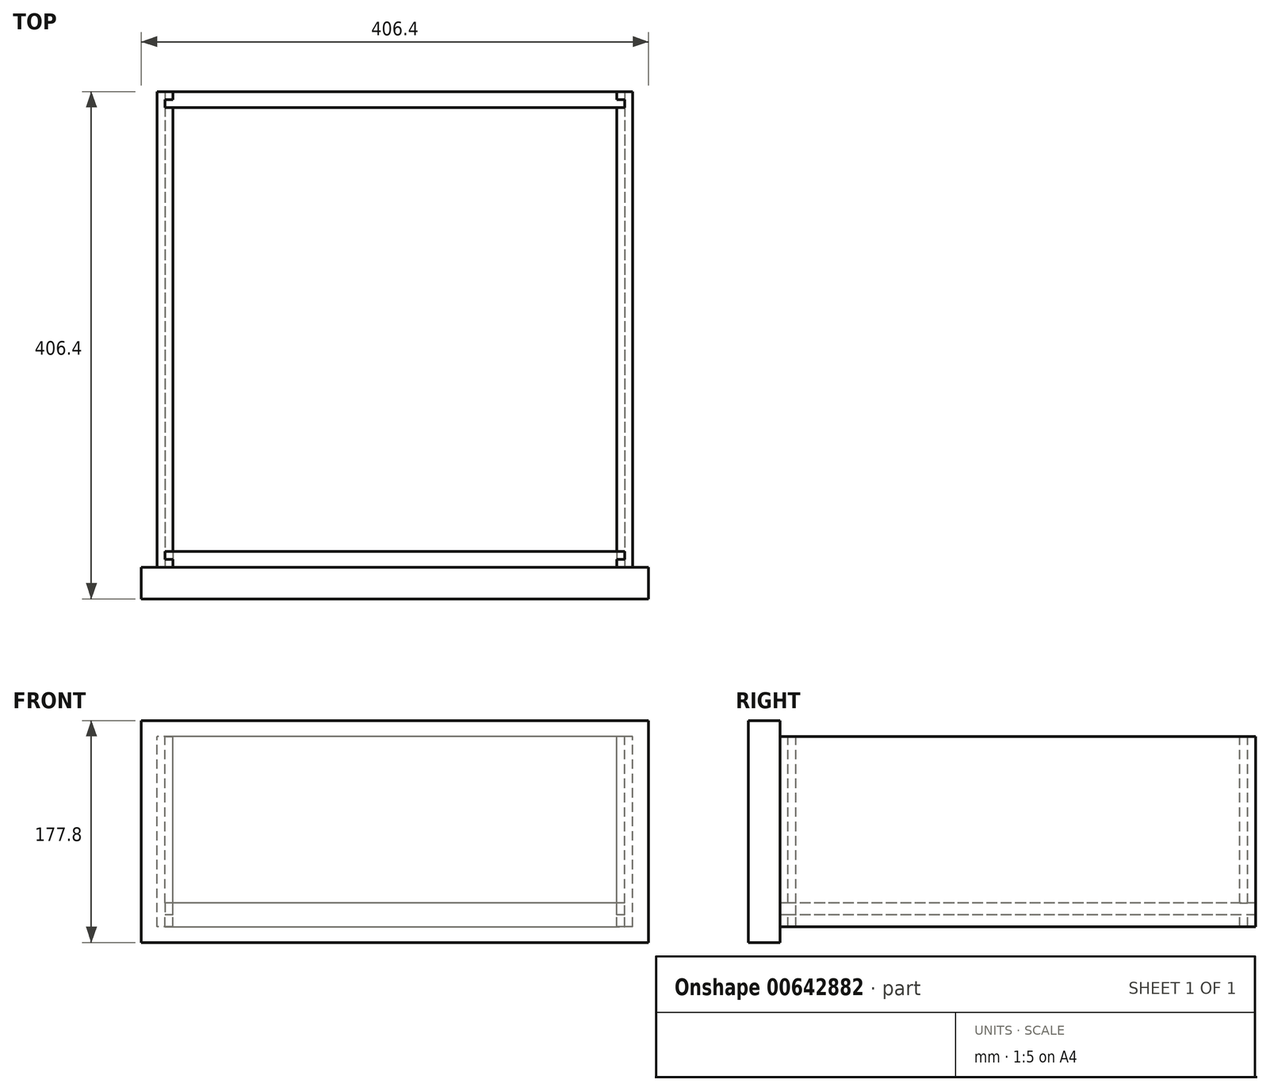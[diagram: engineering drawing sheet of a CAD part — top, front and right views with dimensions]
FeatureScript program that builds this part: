
annotation { "Feature Type Name" : "Feature", "Feature Type Description" : "" }
export const myFeature = defineFeature(function(context is Context, id is Id, definition is map)
    precondition{}
    {
        {
            var Q0;
            Q0=qCreatedBy(makeId("Top.planeOp"),FACE);
            var sketch = newSketch(context, id + "F0", { "sketchPlane" : qUnion([Q0])});
            skLineSegment(sketch, "E0.bottom", {"start": v(190.5, -190.5) * mm, "end": v(-190.5, -190.5) * mm});
            skLineSegment(sketch, "E0.top", {"start": v(190.5, 190.5) * mm, "end": v(-190.5, 190.5) * mm});
            skLineSegment(sketch, "E0.left", {"start": v(190.5, -190.5) * mm, "end": v(190.5, 190.5) * mm});
            skLineSegment(sketch, "E0.right", {"start": v(-190.5, -190.5) * mm, "end": v(-190.5, 190.5) * mm});
            skPoint(sketch, "E0.middle", {"position": v(0, 0) * mm});
            skLineSegment(sketch, "E1.0", {"start": v(-177.8, -190.5) * mm, "end": v(-177.8, -184.15) * mm});
            skLineSegment(sketch, "E2.0", {"start": v(177.8, 177.8) * mm, "end": v(-184.15, 177.8) * mm});
            skLineSegment(sketch, "E2.1", {"start": v(177.8, -177.8) * mm, "end": v(177.8, 177.8) * mm});
            skLineSegment(sketch, "E2.2", {"start": v(177.8, -177.8) * mm, "end": v(-184.15, -177.8) * mm});
            skPoint(sketch, "E3", {"position": v(-177.8, 184.15) * mm});
            skPoint(sketch, "E4", {"position": v(-184.15, 177.8) * mm});
            skLineSegment(sketch, "E5", {"start": v(-184.15, 177.8) * mm, "end": v(-184.15, 184.15) * mm});
            skLineSegment(sketch, "E6", {"start": v(-184.15, 184.15) * mm, "end": v(-177.8, 184.15) * mm});
            skLineSegment(sketch, "E7.trimOffspring", {"start": v(-177.8, 184.15) * mm, "end": v(-177.8, 190.5) * mm});
            skPoint(sketch, "E8.orphan", {"position": v(-190.5, 177.8) * mm});
            skLineSegment(sketch, "E9.MirrorCS", {"start": v(184.15, 184.15) * mm, "end": v(177.8, 184.15) * mm});
            skLineSegment(sketch, "E10.MirrorCS", {"start": v(184.15, 177.8) * mm, "end": v(184.15, 184.15) * mm});
            skLineSegment(sketch, "E11.MirrorCS", {"start": v(177.8, 184.15) * mm, "end": v(177.8, 190.5) * mm});
            skLineSegment(sketch, "E12", {"start": v(177.8, 177.8) * mm, "end": v(184.15, 177.8) * mm});
            skLineSegment(sketch, "E13.MirrorCS", {"start": v(-184.15, -184.15) * mm, "end": v(-177.8, -184.15) * mm});
            skLineSegment(sketch, "E14.MirrorCS", {"start": v(-184.15, -177.8) * mm, "end": v(-184.15, -184.15) * mm});
            skLineSegment(sketch, "E15.MirrorCS", {"start": v(-177.8, -184.15) * mm, "end": v(-177.8, -190.5) * mm});
            skLineSegment(sketch, "E16.MirrorCS", {"start": v(177.8, -184.15) * mm, "end": v(177.8, -190.5) * mm});
            skLineSegment(sketch, "E17.MirrorCS", {"start": v(184.15, -184.15) * mm, "end": v(177.8, -184.15) * mm});
            skLineSegment(sketch, "E18.MirrorCS", {"start": v(184.15, -177.8) * mm, "end": v(184.15, -184.15) * mm});
            skLineSegment(sketch, "E19.MirrorCS", {"start": v(177.8, -177.8) * mm, "end": v(184.15, -177.8) * mm});
            skLineSegment(sketch, "E20.trimOffspring", {"start": v(-177.8, -177.8) * mm, "end": v(-177.8, 177.8) * mm});
            skSolve(sketch);
        }
        {
            var Q0;
            Q0=makeQuery(id+"F0.imprint","IMPRINT",FACE,{"disambiguationData":[TD([[makeQuery(id+"F0.imprint","IMPRINT",EDGE,{"derivedFrom":sQuery(id+"F0.wireOp",EDGE,"E13.MirrorCS")}),1.0]])]});
            extrude(context, id + "F1", {"entities" : qUnion([Q0]), "oppositeDirection" : true, "depth" : 152.4 * mm, "offsetDistance" : 25.4 * mm});
        }
        {
            var Q0;
            {var subQ5=sQuery(id+"F0.wireOp",EDGE,"E0.right");Q0=makeQuery(id+"F0.imprint","IMPRINT",FACE,{"disambiguationData":[TD([[makeQuery(id+"F0.imprint","IMPRINT",EDGE,{"derivedFrom":subQ5}),-1.0]])]});}
            var Q1;
            {var subQ1=sQuery(id+"F0.wireOp",EDGE,"E0.left");Q1=makeQuery(id+"F0.imprint","IMPRINT",FACE,{"disambiguationData":[TD([[makeQuery(id+"F0.imprint","IMPRINT",EDGE,{"derivedFrom":subQ1}),1.0]])]});}
            extrude(context, id + "F2", {"entities" : qUnion([Q0, Q1]), "oppositeDirection" : true, "depth" : 152.4 * mm, "offsetDistance" : 25.4 * mm});
        }
        {
            var Q0;
            {var subQ0=sQuery(id+"F0.wireOp",EDGE,"E5");Q0=makeQuery(id+"F0.imprint","IMPRINT",FACE,{"disambiguationData":[TD([[makeQuery(id+"F0.imprint","IMPRINT",EDGE,{"derivedFrom":subQ0}),-1.0]])]});}
            extrude(context, id + "F3", {"entities" : qUnion([Q0]), "oppositeDirection" : true, "depth" : 133.35 * mm, "offsetDistance" : 25.4 * mm});
        }
        {
            var Q0;
            {var subQ0=sQuery(id+"F0.wireOp",EDGE,"E0.bottom");Q0=makeQuery(id+"F2.opExtrude","SWEPT_FACE",FACE,{"disambiguationData":[OSD([subQ0]),TDD([makeQuery(id+"F0.imprint","IMPRINT",EDGE,{"disambiguationData":[TD([[makeQuery(id+"F0.imprint","INTERSECT",VERTEX,{"derivedFrom":[subQ0,sQuery(id+"F0.wireOp",EDGE,"E0.right")]}),1.0]])],"derivedFrom":subQ0})])]});}
            var sketch = newSketch(context, id + "F4", { "sketchPlane" : qUnion([Q0])});
            skLineSegment(sketch, "E21.0", {"start": v(-177.8, -133.35) * mm, "end": v(-184.15, -133.35) * mm});
            skLineSegment(sketch, "E22.0", {"start": v(-177.8, -142.88) * mm, "end": v(-177.8, -133.35) * mm});
            skLineSegment(sketch, "E23", {"start": v(-184.15, -133.35) * mm, "end": v(-184.15, -142.88) * mm});
            skLineSegment(sketch, "E24", {"start": v(-177.8, -142.88) * mm, "end": v(-184.15, -142.88) * mm});
            skPoint(sketch, "E25.orphan", {"position": v(-177.8, 0) * mm});
            skPoint(sketch, "E26.orphan", {"position": v(184.15, -133.35) * mm});
            skPoint(sketch, "E27.orphan", {"position": v(-177.8, -152.4) * mm});
            skLineSegment(sketch, "E28.MirrorCS", {"start": v(177.8, -133.35) * mm, "end": v(184.15, -133.35) * mm});
            skLineSegment(sketch, "E29.MirrorCS", {"start": v(184.15, -133.35) * mm, "end": v(184.15, -142.88) * mm});
            skLineSegment(sketch, "E30.MirrorCS", {"start": v(177.8, -142.88) * mm, "end": v(184.15, -142.88) * mm});
            skLineSegment(sketch, "E31.MirrorCS", {"start": v(177.8, -142.88) * mm, "end": v(177.8, -133.35) * mm});
            skSolve(sketch);
        }
        {
            var Q0;
            Q0=makeQuery(id+"F4.imprint","IMPRINT",FACE,{"disambiguationData":[TD([[makeQuery(id+"F4.imprint","IMPRINT",EDGE,{"derivedFrom":sQuery(id+"F4.wireOp",EDGE,"E21.0")}),1.0]])]});
            extrude(context, id + "F5", {"entities" : qUnion([Q0]), "operationType" : NewBodyOperationType.REMOVE, "endBound" : BoundingType.THROUGH_ALL, "oppositeDirection" : true, "depth" : 25.4 * mm, "offsetDistance" : 25.4 * mm});
        }
        {
            var Q0;
            Q0=makeQuery(id+"F4.imprint","IMPRINT",FACE,{"disambiguationData":[TD([[makeQuery(id+"F4.imprint","IMPRINT",EDGE,{"derivedFrom":sQuery(id+"F4.wireOp",EDGE,"E28.MirrorCS")}),-1.0]])]});
            extrude(context, id + "F6", {"entities" : qUnion([Q0]), "operationType" : NewBodyOperationType.REMOVE, "endBound" : BoundingType.THROUGH_ALL, "oppositeDirection" : true, "depth" : 25.4 * mm, "offsetDistance" : 25.4 * mm});
        }
        {
            var Q0;
            {var subQ3=sQuery(id+"F4.wireOp",EDGE,"E21.0");Q0=makeQuery(id+"F4.imprint","IMPRINT",FACE,{"disambiguationData":[TD([[makeQuery(id+"F4.imprint","IMPRINT",EDGE,{"derivedFrom":subQ3}),-1.0]])]});}
            var sketch = newSketch(context, id + "F7", { "sketchPlane" : qUnion([Q0])});
            skLineSegment(sketch, "E32.0", {"start": v(184.15, -133.35) * mm, "end": v(-184.15, -133.35) * mm});
            skLineSegment(sketch, "E33.0", {"start": v(-184.15, -133.35) * mm, "end": v(-184.15, -142.88) * mm});
            skLineSegment(sketch, "E34.0", {"start": v(-177.8, -142.88) * mm, "end": v(-184.15, -142.88) * mm});
            skLineSegment(sketch, "E35.0", {"start": v(184.15, -133.35) * mm, "end": v(184.15, -142.88) * mm});
            skLineSegment(sketch, "E36.0", {"start": v(177.8, -142.88) * mm, "end": v(184.15, -142.88) * mm});
            skLineSegment(sketch, "E37.0", {"start": v(-177.8, -152.4) * mm, "end": v(-177.8, -142.88) * mm});
            skLineSegment(sketch, "E38.0", {"start": v(177.8, -152.4) * mm, "end": v(177.8, -142.88) * mm});
            skLineSegment(sketch, "E39", {"start": v(-177.8, -152.4) * mm, "end": v(177.8, -152.4) * mm});
            skSolve(sketch);
        }
        {
            var Q0;
            {var subQ0=sQuery(id+"F7.wireOp",EDGE,"E33.0");Q0=makeQuery(id+"F7.imprint","IMPRINT",FACE,{"disambiguationData":[TD([[makeQuery(id+"F7.imprint","IMPRINT",EDGE,{"derivedFrom":subQ0}),1.0]])]});}
            var Q1;
            {var subQ0=sQuery(id+"F0.wireOp",EDGE,"E0.top");Q1=makeQuery(id+"F2.opExtrude","SWEPT_FACE",FACE,{"disambiguationData":[OSD([subQ0]),TDD([makeQuery(id+"F0.imprint","IMPRINT",EDGE,{"disambiguationData":[TD([[makeQuery(id+"F0.imprint","INTERSECT",VERTEX,{"derivedFrom":[subQ0,sQuery(id+"F0.wireOp",EDGE,"E0.left")]}),-1.0]])],"derivedFrom":subQ0})])]});}
            extrude(context, id + "F8", {"entities" : qUnion([Q0]), "endBound" : BoundingType.UP_TO_SURFACE, "oppositeDirection" : true, "depth" : 25.4 * mm, "endBoundEntityFace" : qUnion([Q1]), "offsetDistance" : 25.4 * mm});
        }
        {
            var Q0;
            Q0=makeQuery(id+"F1.opExtrude","SWEPT_FACE",FACE,{"disambiguationData":[OSD([sQuery(id+"F0.wireOp",EDGE,"E0.bottom")])]});
            var sketch = newSketch(context, id + "F9", { "sketchPlane" : qUnion([Q0])});
            skLineSegment(sketch, "E40.0", {"start": v(203.2, 12.7) * mm, "end": v(177.8, 12.7) * mm});
            skLineSegment(sketch, "E40.1", {"start": v(203.2, -165.1) * mm, "end": v(203.2, 12.7) * mm});
            skLineSegment(sketch, "E40.2", {"start": v(177.8, 12.7) * mm, "end": v(-177.8, 12.7) * mm});
            skLineSegment(sketch, "E40.3", {"start": v(203.2, -165.1) * mm, "end": v(177.8, -165.1) * mm});
            skLineSegment(sketch, "E40.4", {"start": v(-177.8, 12.7) * mm, "end": v(-203.2, 12.7) * mm});
            skLineSegment(sketch, "E40.5", {"start": v(-203.2, -165.1) * mm, "end": v(-203.2, 12.7) * mm});
            skLineSegment(sketch, "E40.6", {"start": v(-177.8, -165.1) * mm, "end": v(-203.2, -165.1) * mm});
            skLineSegment(sketch, "E40.7", {"start": v(177.8, -165.1) * mm, "end": v(-177.8, -165.1) * mm});
            skPoint(sketch, "E41.0.end.orphan", {"position": v(-177.8, 0) * mm});
            skPoint(sketch, "E41.0.start.orphan", {"position": v(177.8, 0) * mm});
            skPoint(sketch, "E42.0.end.orphan", {"position": v(-190.5, 0) * mm});
            skPoint(sketch, "E43.0.end.orphan", {"position": v(-190.5, -152.4) * mm});
            skPoint(sketch, "E43.0.start.orphan", {"position": v(-177.8, -152.4) * mm});
            skPoint(sketch, "E44.0.start.orphan", {"position": v(177.8, -152.4) * mm});
            skPoint(sketch, "E45.0.start.orphan", {"position": v(190.5, -152.4) * mm});
            skPoint(sketch, "E46.0.start.orphan", {"position": v(190.5, 0) * mm});
            skSolve(sketch);
        }
        {
            var Q0;
            Q0=makeQuery(id+"F9.imprint","IMPRINT",FACE,{"disambiguationData":[TD([[makeQuery(id+"F9.imprint","IMPRINT",EDGE,{"derivedFrom":sQuery(id+"F9.wireOp",EDGE,"E40.0")}),1.0]])]});
            var Q1;
            {var subQ0=sQuery(id+"F0.wireOp",EDGE,"E0.bottom");Q1=makeQuery(id+"F9.imprint","IMPRINT",FACE,{"disambiguationData":[TD([[makeQuery(id+"F9.imprint","IMPRINT",EDGE,{"derivedFrom":makeQuery(id+"F1.opExtrude","CAP_EDGE",EDGE,{"disambiguationData":[OSD([subQ0])],"isStart":true})}),1.0]])]});}
            extrude(context, id + "F10", {"entities" : qUnion([Q0, Q1]), "depth" : 25.4 * mm, "offsetDistance" : 25.4 * mm});
        }
    });
